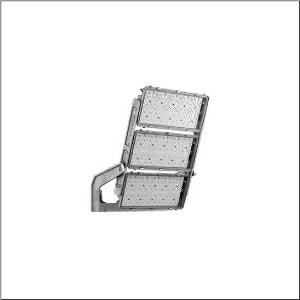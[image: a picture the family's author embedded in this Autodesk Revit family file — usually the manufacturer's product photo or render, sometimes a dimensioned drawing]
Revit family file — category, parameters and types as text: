
# Revit family: floodlight_fl_11_maxi_pro_remote___pl64blc_5xa779428w01aa_23f9
name_source: partatom
category: Lighting Fixtures
units: mm (PartAtom-declared; Revit-internal decimal feet)

## family parameters
Cut with Voids When Loaded = No
Host = Face
Light Source = No
Part Type = Normal
Room Calculation Point = No
Round Connector Dimension = Use Diameter
Shared = No

## types (1)
- --- (1 x LED, 127830 lm, 1516.9 W, 5700K)
    Apparent Load = 1517 VA
    CIE Flux Codes = 28 83 99 100 100
    Color Rendering = 80
    Color Temperature = 5700K
    Default Elevation = 1800 mm
    Description = Floodlight FL 11  maxi  pro Remote floodlight; light control with lens of PMMA; cover panel of toughened safety glass, transparent; light distribution: PL64BLC, asymmetric direct distribution, LEDcolour temperature: 5700K, rated luminous flux: 127.830lm, colour rendering: CRI > 80, light colour: 857; luminous efficacy: 84lm/W; brightness control: DALI 2 (1 DALI address); with terminal, 8-pole, max. 2.5mm², mains connection: 220..240V/380..400V AC, 50/60Hz, surge voltage resistance: line to ground: 10kV, dimming range 10..100%, dustproof LED module, LED unit replaceable without ESD environment, no afterglow with DALI off / DMX off command, ECG replaceable separately; 1517W floodlight with 3x LED unit of diecast aluminium, coated grey; length: 1.003mm / width: 651mm / height: 338mm; mounting bracket, of diecast aluminium, uncoated, natural, equipment: Power, protection rating (complete): IP66; insulation class (complete): insulation class I (protective earthing); certification: CE, ENEC, VDE; ball protection: ball impact resistant, impact resistance: IK07; only for outdoor installations, rated ambient temperature 10°C, permissible operating ambient temperature: -40..+30°C, permissible storage temperature: -40..+85°Cpackaging unit: 1 piece

Light Distribution: PL64BLC
    Height = 320 mm
    Lamp = 1 x LED
    Lamp Light Flux = 127830 lm
    Lamp Power = 1516.9 W
    Lamp count = 1
    Length = 1002 mm
    Luminous efficacy = 84 lm/W
    Manufacturer = Siteco
    ModVariant = No
    Model = 5XA779428W01AA
    Mounting Place = Ceiling
    Mounting Type = Surface mounted
    Number of Poles = 1
    OnlyDefault = Yes
    Power Factor = 1
    Product Name = Floodlight FL 11 maxi pro Remote | PL64BLC
    Product group = floodlight | ceiling mounted
    ProductGroupID = 301
    Protection Class = Protection class I
    Protection Degree = IP 66
    RLX_Detail_Level = 1
    RLX_Emergency_Light_Flux = 0 lm
    RLX_Emergency_Type = 0
    RLX_Emergency_Type_DB = No
    RlxData = <blob elided: 52133 chars, md5=edea222c>
    Socket = socket
    Standby Power = 0 W
    System Light Flux = 127830 lm
    System Power = 1517 W
    Type Comments = factory setting: luminous flux: 100 % | dim-lin: 254 | 1070 mA
    Type Image = l_1349141.jpg
    URL = http://relux.com
    VarID = @adj_080232
    Voltage = 0 V
    Weight = 0.00 kg
    Width = 655 mm

## geometry (parser evidence)
native form markers: Blend x4, Sweep x12
no freeform markers — native parametric forms only
